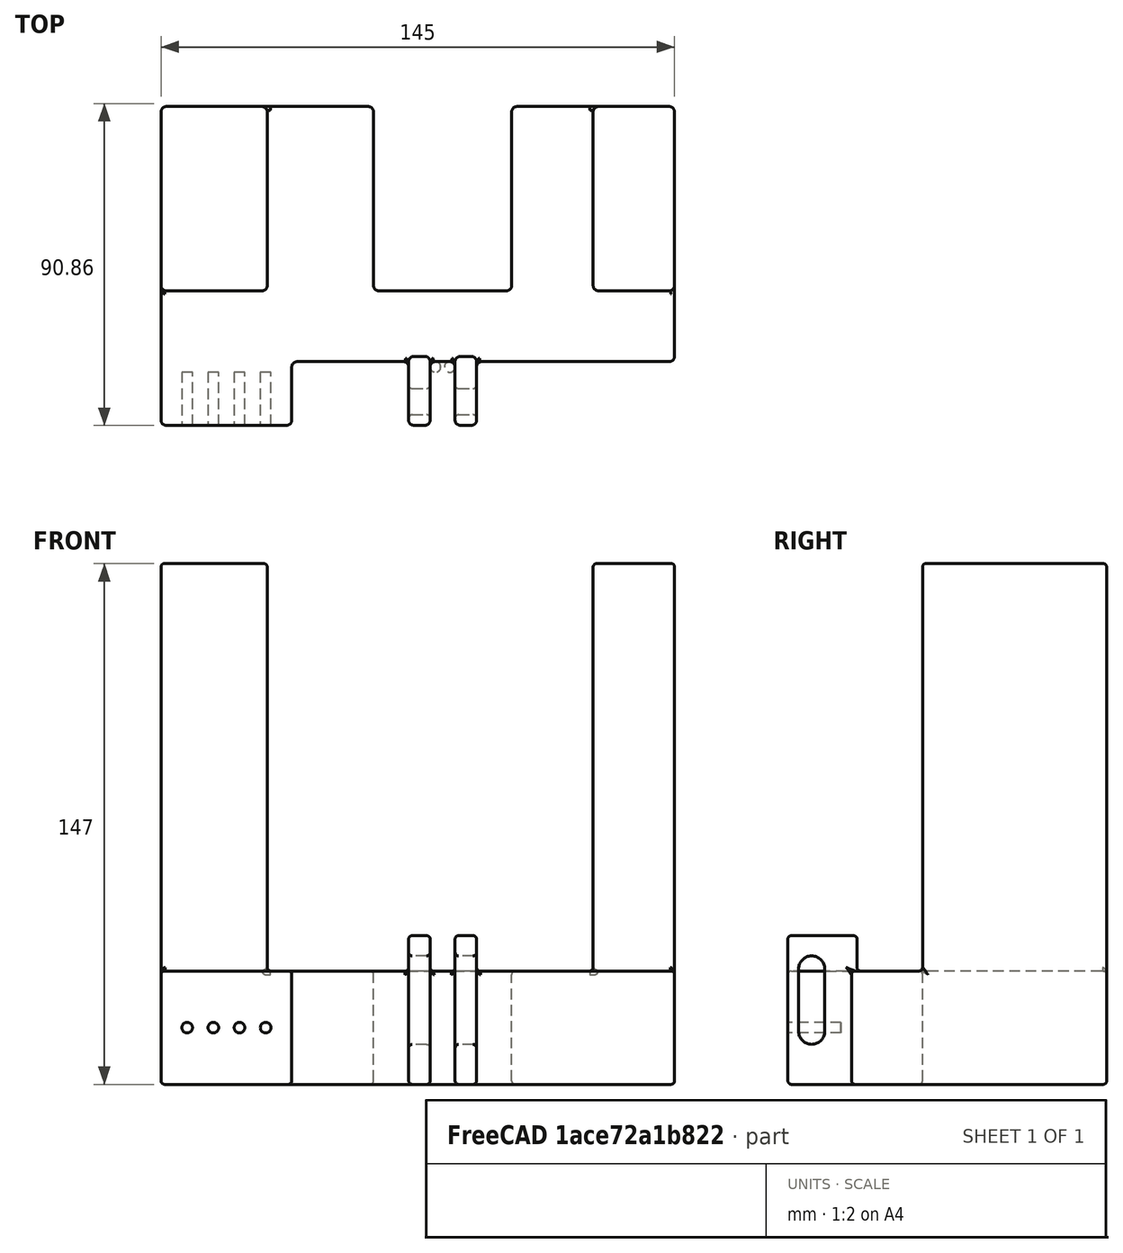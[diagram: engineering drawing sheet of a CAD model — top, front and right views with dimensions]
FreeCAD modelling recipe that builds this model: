
FCSTD DOCUMENT  (FreeCAD 1.0RUnknown)
Label: water-valve-support-v3
License: All rights reserved
LicenseURL: https://en.wikipedia.org/wiki/All_rights_reserved
objects: Sketcher::SketchObject×5, PartDesign::Pad×4, PartDesign::Fillet×4, PartDesign::Pocket×2, PartDesign::Body×1
note: 41 computed .brp shape members not serialized (recipe doc carries the construction recipe); baked Part::Feature solids carry a one-line shape summary decoded from their .brp

FEATURE [Sketcher::SketchObject] Sketch
  ArcFitTolerance = 1e-06
  AttachmentSupport = -> [XY_Plane]
  FullyConstrained = false
  MakeInternals = false
  MapMode = 5
  sketch-geometry (67):
    g0: LineSegment StartX=0 StartY=1.5 StartZ=0 EndX=0 EndY=38 EndZ=0
    g1: LineSegment StartX=0 StartY=38 StartZ=0 EndX=0 EndY=88.5 EndZ=0
    g2: LineSegment StartX=1.5 StartY=90 StartZ=0 EndX=58.5 EndY=90 EndZ=0
    g3: LineSegment StartX=60 StartY=88.5 StartZ=0 EndX=60 EndY=39.5 EndZ=0
    g4: LineSegment StartX=61.5 StartY=38 StartZ=0 EndX=97.5 EndY=38 EndZ=0
    g5: LineSegment StartX=99 StartY=39.5 StartZ=0 EndX=99 EndY=88.5 EndZ=0
    g6: LineSegment StartX=100.5 StartY=90 StartZ=0 EndX=143.5 EndY=90 EndZ=0
    g7: LineSegment StartX=145 StartY=88.5 StartZ=0 EndX=145 EndY=19.5 EndZ=0
    g8: LineSegment [constr] StartX=143.506 StartY=0 StartZ=0 EndX=118.575 EndY=0 EndZ=0
    g9: ArcOfCircle CenterX=1.5 CenterY=88.5 CenterZ=0 NormalX=0 NormalY=0 NormalZ=1 AngleXU=0 Radius=1.5 StartAngle=1.5708 EndAngle=3.14159
    g10: GeomPoint [constr] X=0 Y=90 Z=0
    g11: ArcOfCircle CenterX=58.5 CenterY=88.5 CenterZ=0 NormalX=0 NormalY=0 NormalZ=1 AngleXU=0 Radius=1.5 StartAngle=1.1e-15 EndAngle=1.5708
    g12: GeomPoint [constr] X=60 Y=90 Z=0
    g13: ArcOfCircle CenterX=61.5 CenterY=39.5 CenterZ=0 NormalX=0 NormalY=0 NormalZ=1 AngleXU=0 Radius=1.5 StartAngle=3.14159 EndAngle=4.71239
    g14: GeomPoint [constr] X=60 Y=38 Z=0
    g15: ArcOfCircle CenterX=97.5 CenterY=39.5 CenterZ=0 NormalX=0 NormalY=0 NormalZ=1 AngleXU=0 Radius=1.5 StartAngle=4.71239 EndAngle=6.28319
    g16: GeomPoint [constr] X=99 Y=38 Z=0
    g17: ArcOfCircle CenterX=100.5 CenterY=88.5 CenterZ=0 NormalX=0 NormalY=0 NormalZ=1 AngleXU=0 Radius=1.5 StartAngle=1.5708 EndAngle=3.14159
    g18: GeomPoint [constr] X=99 Y=90 Z=0
    g19: ArcOfCircle CenterX=143.5 CenterY=88.5 CenterZ=0 NormalX=0 NormalY=0 NormalZ=1 AngleXU=0 Radius=1.5 StartAngle=-4.4e-15 EndAngle=1.5708
    g20: GeomPoint [constr] X=145 Y=90 Z=0
    g21: ArcOfCircle [constr] CenterX=143.506 CenterY=1.5 CenterZ=0 NormalX=0 NormalY=0 NormalZ=1 AngleXU=0 Radius=1.5 StartAngle=4.71239 EndAngle=6.28336
    g22: GeomPoint [constr] X=145 Y=0 Z=0
    g23: ArcOfCircle CenterX=1.5 CenterY=1.5 CenterZ=0 NormalX=0 NormalY=0 NormalZ=1 AngleXU=0 Radius=1.5 StartAngle=3.14159 EndAngle=4.71239
    g24: GeomPoint [constr] X=0 Y=0 Z=0
    g25: GeomPoint [constr] X=79.5 Y=38 Z=0
    g26: LineSegment [constr] StartX=79.5 StartY=38 StartZ=0 EndX=79.5 EndY=0 EndZ=0
    g27: LineSegment StartX=75.975 StartY=1.5 StartZ=0 EndX=75.975 EndY=16.5 EndZ=0
    g28: LineSegment StartX=77.475 StartY=18 StartZ=0 EndX=81.525 EndY=18 EndZ=0
    g29: LineSegment StartX=83.025 StartY=1.5 StartZ=0 EndX=83.025 EndY=16.5 EndZ=0
    g30: GeomPoint [constr] X=79.5 Y=18 Z=0
    g31: LineSegment StartX=36.925 StartY=16.5 StartZ=0 EndX=36.925 EndY=1.5 EndZ=0
    g32: LineSegment StartX=69.925 StartY=1.5 StartZ=0 EndX=69.925 EndY=16.5 EndZ=0
    g33: LineSegment StartX=68.425 StartY=18 StartZ=0 EndX=38.425 EndY=18 EndZ=0
    g34: LineSegment StartX=89.075 StartY=16.5 StartZ=0 EndX=89.075 EndY=1.5 EndZ=0
    g35: LineSegment [constr] StartX=117.075 StartY=1.5 StartZ=0 EndX=117.075 EndY=16.5 EndZ=0
    g36: LineSegment StartX=115.575 StartY=18 StartZ=0 EndX=90.575 EndY=18 EndZ=0
    g37: LineSegment StartX=35.425 StartY=0 StartZ=0 EndX=1.5 EndY=0 EndZ=0
    g38: LineSegment StartX=74.475 StartY=0 StartZ=0 EndX=71.425 EndY=0 EndZ=0
    g39: LineSegment StartX=87.575 StartY=0 StartZ=0 EndX=84.525 EndY=0 EndZ=0
    g40: ArcOfCircle CenterX=35.425 CenterY=1.5 CenterZ=0 NormalX=0 NormalY=0 NormalZ=1 AngleXU=0 Radius=1.5 StartAngle=4.71239 EndAngle=6.28319
    g41: ArcOfCircle CenterX=71.425 CenterY=1.5 CenterZ=0 NormalX=0 NormalY=0 NormalZ=1 AngleXU=0 Radius=1.5 StartAngle=3.14159 EndAngle=4.71239
    g42: GeomPoint [constr] X=69.925 Y=0 Z=0
    g43: ArcOfCircle CenterX=74.475 CenterY=1.5 CenterZ=0 NormalX=0 NormalY=0 NormalZ=1 AngleXU=0 Radius=1.5 StartAngle=4.71239 EndAngle=6.28319
    g44: ArcOfCircle CenterX=84.525 CenterY=1.5 CenterZ=0 NormalX=0 NormalY=0 NormalZ=1 AngleXU=0 Radius=1.5 StartAngle=3.14159 EndAngle=4.71239
    g45: GeomPoint [constr] X=83.025 Y=0 Z=0
    g46: ArcOfCircle CenterX=87.575 CenterY=1.5 CenterZ=0 NormalX=0 NormalY=0 NormalZ=1 AngleXU=0 Radius=1.5 StartAngle=4.71239 EndAngle=6.28319
    g47: ArcOfCircle [constr] CenterX=118.575 CenterY=1.5 CenterZ=0 NormalX=0 NormalY=0 NormalZ=1 AngleXU=0 Radius=1.5 StartAngle=3.14159 EndAngle=4.71239
    g48: ArcOfCircle CenterX=38.425 CenterY=16.5 CenterZ=0 NormalX=0 NormalY=0 NormalZ=1 AngleXU=0 Radius=1.5 StartAngle=1.5708 EndAngle=3.14159
    g49: GeomPoint [constr] X=36.925 Y=18 Z=0
    g50: GeomPoint [constr] X=69.925 Y=18 Z=0
    g51: GeomPoint [constr] X=75.975 Y=18 Z=0
    g52: GeomPoint [constr] X=83.025 Y=18 Z=0
    g53: GeomPoint [constr] X=89.075 Y=18 Z=0
    g54: ArcOfCircle [constr] CenterX=115.575 CenterY=16.5 CenterZ=0 NormalX=0 NormalY=0 NormalZ=1 AngleXU=0 Radius=1.5 StartAngle=0 EndAngle=1.5708
    g55: GeomPoint [constr] X=117.075 Y=18 Z=0
    g56: ArcOfCircle CenterX=68.425 CenterY=16.5 CenterZ=0 NormalX=0 NormalY=0 NormalZ=1 AngleXU=0 Radius=1.5 StartAngle=0 EndAngle=1.5708
    g57: GeomPoint [constr] X=69.925 Y=18 Z=0
    g58: ArcOfCircle CenterX=77.475 CenterY=16.5 CenterZ=0 NormalX=0 NormalY=0 NormalZ=1 AngleXU=0 Radius=1.5 StartAngle=1.5708 EndAngle=3.14159
    g59: GeomPoint [constr] X=75.975 Y=18 Z=0
    g60: ArcOfCircle CenterX=81.525 CenterY=16.5 CenterZ=0 NormalX=0 NormalY=0 NormalZ=1 AngleXU=0 Radius=1.5 StartAngle=4e-16 EndAngle=1.5708
    g61: GeomPoint [constr] X=83.025 Y=18 Z=0
    g62: ArcOfCircle CenterX=90.575 CenterY=16.5 CenterZ=0 NormalX=0 NormalY=0 NormalZ=1 AngleXU=0 Radius=1.5 StartAngle=1.5708 EndAngle=3.14159
    g63: GeomPoint [constr] X=89.075 Y=18 Z=0
    g64: LineSegment StartX=115.575 StartY=18 StartZ=0 EndX=143.5 EndY=18 EndZ=0
    g65: ArcOfCircle CenterX=143.5 CenterY=19.5 CenterZ=0 NormalX=0 NormalY=0 NormalZ=1 AngleXU=0 Radius=1.5 StartAngle=4.71239 EndAngle=6.28319
    g66: LineSegment [constr] StartX=145 StartY=19.5 StartZ=0 EndX=145 EndY=1.36507 EndZ=0
  constraints (152):
    c: Coincident(g24,g-1)
    c: PointOnObject(g0,g-2)
    c: Vertical(g1)
    c: Horizontal(g2)
    c: Vertical(g3)
    c: Horizontal(g4)
    c: Vertical(g5)
    c: Horizontal(g6)
    c: Vertical(g7)
    c: PointOnObject(g22,g-1)
    c: Horizontal(g1,g14)
    c: DistanceX(g24,g22) = 145
    c: Distance(g24,g0) = 38
    c: DistanceX(g16,g22) = 46
    c: DistanceX(g14,g16) = 39
    c: Distance(g12,g14) = 52
    c: Coincident(g1,g0)
    c: PointOnObject(g10,g1)
    c: PointOnObject(g10,g2)
    c: Tangent(g1,g9) = 1.5708
    c: Tangent(g2,g9) = 1.5708
    c: PointOnObject(g12,g2)
    c: PointOnObject(g12,g3)
    c: Tangent(g2,g11) = 1.5708
    c: Tangent(g3,g11) = 1.5708
    c: PointOnObject(g14,g4)
    c: PointOnObject(g14,g3)
    c: Tangent(g4,g13) = -1.5708
    c: Tangent(g3,g13) = -1.5708
    c: PointOnObject(g16,g5)
    c: PointOnObject(g16,g4)
    c: Tangent(g5,g15) = -1.5708
    c: Tangent(g4,g15) = -1.5708
    c: PointOnObject(g18,g5)
    c: PointOnObject(g18,g6)
    c: Tangent(g5,g17) = 1.5708
    c: Tangent(g6,g17) = 1.5708
    c: PointOnObject(g20,g6)
    c: PointOnObject(g20,g7)
    c: Tangent(g6,g19) = 1.5708
    c: Tangent(g7,g19) = 1.5708
    c: PointOnObject(g22,g8)
    c: PointOnObject(g22,g7)
    c: Tangent(g8,g21) = 1.5708
    c: PointOnObject(g24,g37)
    c: PointOnObject(g24,g0)
    c: Coincident(g37,g23) = 1.5708
    c: Tangent(g0,g23) = 1.5708
    c: Equal(g9,g11)
    c: Equal(g11,g13)
    c: Equal(g13,g15)
    c: Equal(g15,g17)
    c: Equal(g17,g19)
    c: Equal(g19,g21)
    c: Equal(g21,g23)
    c: Radius(g9) = 1.5
    c: Horizontal(g11,g17)
    c: Symmetric(g4,g4,g25)
    c: Coincident(g26,g25)
    c: Vertical(g26)
    c: Vertical(g27)
    c: Horizontal(g28)
    c: Vertical(g29)
    c: Symmetric(g51,g52,g30)
    c: PointOnObject(g30,g26)
    c: Vertical(g31)
    c: Vertical(g32)
    c: Horizontal(g33)
    c: Vertical(g34)
    c: Vertical(g35)
    c: Horizontal(g36)
    c: Horizontal(g53,g30)
    c: Horizontal(g30,g50)
    c: Tangent(g37,g40) = 1.5708
    c: Tangent(g31,g40) = 1.5708
    c: PointOnObject(g42,g32)
    c: PointOnObject(g42,g38)
    c: Tangent(g32,g41) = 1.5708
    c: Tangent(g38,g41) = 1.5708
    c: Tangent(g38,g43) = 1.5708
    c: Tangent(g27,g43) = -1.5708
    c: PointOnObject(g45,g29)
    c: PointOnObject(g45,g39)
    c: Tangent(g29,g44) = 1.5708
    c: Tangent(g39,g44) = 1.5708
    c: Tangent(g39,g46) = 1.5708
    c: Tangent(g34,g46) = 1.5708
    c: Tangent(g35,g47) = 1.5708
    c: Tangent(g8,g47) = 1.5708
    c: PointOnObject(g49,g31)
    c: PointOnObject(g49,g33)
    c: Tangent(g31,g48) = -1.5708
    c: Tangent(g33,g48) = -1.5708
    c: PointOnObject(g53,g34)
    c: PointOnObject(g53,g36)
    c: PointOnObject(g55,g36)
    c: PointOnObject(g55,g35)
    c: Tangent(g36,g54) = -1.5708
    c: Tangent(g35,g54) = -1.5708
    c: Equal(g40,g48)
    c: Equal(g41,g43)
    c: Equal(g44,g46)
    c: Equal(g54,g47)
    c: Horizontal(g38)
    c: Horizontal(g8)
    c: Horizontal(g39)
    c: Horizontal(g39,g8)
    c: Horizontal(g8,g38)
    c: Horizontal(g38,g26)
    c: Horizontal(g37,g38)
    c: Equal(g40,g23)
    c: Equal(g38,g39)
    c: Distance(g27,g32) = 6.05
    c: Distance(g49,g-1) = 18
    c: Distance(g29,g27) = 7.05
    c: Coincident(g57,g50)
    c: Coincident(g59,g51)
    c: Coincident(g61,g52)
    c: Equal(g46,g41)
    c: Equal(g43,g40)
    c: Equal(g47,g48)
    c: PointOnObject(g57,g33)
    c: PointOnObject(g57,g32)
    c: Tangent(g33,g56) = -1.5708
    c: Tangent(g32,g56) = -1.5708
    c: PointOnObject(g59,g27)
    c: PointOnObject(g59,g28)
    c: Tangent(g27,g58) = 1.5708
    c: Tangent(g28,g58) = 1.5708
    c: PointOnObject(g61,g28)
    c: PointOnObject(g61,g29)
    c: Tangent(g28,g60) = 1.5708
    c: Tangent(g29,g60) = -1.5708
    c: PointOnObject(g63,g34)
    c: PointOnObject(g63,g36)
    c: Tangent(g34,g62) = -1.5708
    c: Tangent(g36,g62) = -1.5708
    c: Equal(g62,g60)
    c: Equal(g60,g58)
    c: Equal(g58,g56)
    c: Equal(g56,g41)
    c: DistanceX(g33,g33) = 30
    c: DistanceX(g36,g36) = 25
    c: Horizontal(g23,g40)
    c: Coincident(g64,g36)
    c: Horizontal(g64)
    c: Tangent(g7,g65) = 1.5708
    c: Tangent(g64,g65) = -1.5708
    c: Equal(g65,g54)
    c: Tangent(g66,g65) = 1.5708
    c: PointOnObject(g66,g21)
    c: Vertical(g66)
FEATURE [PartDesign::Pad] Pad
  Direction = (0,0,1)
  Length = 32
  Length2 = 10
  Profile = -> Sketch
  ReferenceAxis = -> Sketch [N_Axis]
  Refine = true
  Suppressed = false
  Type = 0
FEATURE [Sketcher::SketchObject] Sketch001
  ArcFitTolerance = 1e-06
  AttachmentSupport = -> [Pad]
  ExternalGeometry = -> [Pad]
  FullyConstrained = true
  MakeInternals = false
  MapMode = 5
  Placement = pos=(0,0,32) rot=(0,0,1;0rad)
  sketch-geometry (28):
    g0: LineSegment StartX=2.82e-13 StartY=88.5 StartZ=0 EndX=2.82e-13 EndY=39.5 EndZ=0
    g1: LineSegment StartX=1.5 StartY=38 StartZ=0 EndX=28.5 EndY=38 EndZ=0
    g2: LineSegment StartX=28.5 StartY=90 StartZ=0 EndX=1.5 EndY=90 EndZ=0
    g3: LineSegment StartX=123.5 StartY=38 StartZ=0 EndX=143.5 EndY=38 EndZ=0
    g4: LineSegment StartX=145 StartY=39.5 StartZ=0 EndX=145 EndY=88.5 EndZ=0
    g5: LineSegment StartX=143.5 StartY=90 StartZ=0 EndX=123.5 EndY=90 EndZ=0
    g6: ArcOfCircle CenterX=1.5 CenterY=88.5 CenterZ=0 NormalX=0 NormalY=0 NormalZ=1 AngleXU=0 Radius=1.5 StartAngle=1.5708 EndAngle=3.14159
    g7: GeomPoint [constr] X=6.1e-15 Y=90 Z=0
    g8: ArcOfCircle CenterX=1.5 CenterY=39.5 CenterZ=0 NormalX=0 NormalY=0 NormalZ=1 AngleXU=0 Radius=1.5 StartAngle=3.14159 EndAngle=4.71239
    g9: GeomPoint [constr] X=6.1e-15 Y=38 Z=0
    g10: ArcOfCircle CenterX=143.5 CenterY=88.5 CenterZ=0 NormalX=0 NormalY=0 NormalZ=1 AngleXU=0 Radius=1.5 StartAngle=3.04e-14 EndAngle=1.5708
    g11: GeomPoint [constr] X=145 Y=90 Z=0
    g12: ArcOfCircle CenterX=143.5 CenterY=39.5 CenterZ=0 NormalX=0 NormalY=0 NormalZ=1 AngleXU=0 Radius=1.5 StartAngle=4.71239 EndAngle=6.28319
    g13: GeomPoint [constr] X=145 Y=38 Z=0
    g14: GeomPoint [constr] X=30 Y=90 Z=0
    g15: GeomPoint [constr] X=122 Y=90 Z=0
    g16: LineSegment StartX=30 StartY=88.5 StartZ=0 EndX=30 EndY=39.5 EndZ=0
    g17: LineSegment StartX=122 StartY=88.5 StartZ=0 EndX=122 EndY=39.5 EndZ=0
    g18: GeomPoint [constr] X=30 Y=90 Z=0
    g19: GeomPoint [constr] X=122 Y=90 Z=0
    g20: ArcOfCircle CenterX=28.5 CenterY=88.5 CenterZ=0 NormalX=0 NormalY=0 NormalZ=1 AngleXU=0 Radius=1.5 StartAngle=1.119e-13 EndAngle=1.5708
    g21: GeomPoint [constr] X=30 Y=90 Z=0
    g22: ArcOfCircle CenterX=28.5 CenterY=39.5 CenterZ=0 NormalX=0 NormalY=0 NormalZ=1 AngleXU=0 Radius=1.5 StartAngle=4.71239 EndAngle=6.28319
    g23: GeomPoint [constr] X=30 Y=38 Z=0
    g24: ArcOfCircle CenterX=123.5 CenterY=88.5 CenterZ=0 NormalX=0 NormalY=0 NormalZ=1 AngleXU=0 Radius=1.5 StartAngle=1.5708 EndAngle=3.14159
    g25: GeomPoint [constr] X=122 Y=90 Z=0
    g26: ArcOfCircle CenterX=123.5 CenterY=39.5 CenterZ=0 NormalX=0 NormalY=0 NormalZ=1 AngleXU=0 Radius=1.5 StartAngle=3.14159 EndAngle=4.71239
    g27: GeomPoint [constr] X=122 Y=38 Z=0
  constraints (56):
    c: Vertical(g0)
    c: Horizontal(g1)
    c: Horizontal(g2)
    c: Vertical(g4)
    c: Horizontal(g3)
    c: Horizontal(g5)
    c: PointOnObject(g7,g0)
    c: PointOnObject(g7,g2)
    c: Tangent(g0,g6) = -1.5708
    c: Tangent(g2,g6) = -1.5708
    c: PointOnObject(g9,g0)
    c: PointOnObject(g9,g1)
    c: Tangent(g0,g8) = -1.5708
    c: Tangent(g1,g8) = -1.5708
    c: PointOnObject(g11,g4)
    c: PointOnObject(g11,g5)
    c: Tangent(g4,g10) = -1.5708
    c: Tangent(g5,g10) = -1.5708
    c: PointOnObject(g13,g3)
    c: PointOnObject(g13,g4)
    c: Tangent(g3,g12) = -1.5708
    c: Tangent(g4,g12) = -1.5708
    c: Coincident(g6,g-4)
    c: Coincident(g10,g-14)
    c: Coincident(g21,g14)
    c: Coincident(g25,g15)
    c: Symmetric(g-3,g-3,g18)
    c: Symmetric(g-13,g-13,g19)
    c: Coincident(g21,g18)
    c: Vertical(g16)
    c: Horizontal(g27,g-10)
    c: Horizontal(g-10,g23)
    c: Coincident(g15,g19)
    c: Vertical(g17)
    c: PointOnObject(g21,g2)
    c: PointOnObject(g21,g16)
    c: Tangent(g2,g20) = -1.5708
    c: Tangent(g16,g20) = 1.5708
    c: PointOnObject(g23,g16)
    c: PointOnObject(g23,g1)
    c: Tangent(g16,g22) = 1.5708
    c: Tangent(g1,g22) = -1.5708
    c: PointOnObject(g25,g17)
    c: PointOnObject(g25,g5)
    c: Tangent(g17,g24) = -1.5708
    c: Tangent(g5,g24) = -1.5708
    c: PointOnObject(g27,g3)
    c: PointOnObject(g27,g17)
    c: Tangent(g3,g26) = -1.5708
    c: Tangent(g17,g26) = -1.5708
    c: Equal(g20,g8)
    c: Equal(g8,g22)
    c: Equal(g22,g24)
    c: Equal(g24,g26)
    c: Equal(g26,g12)
    c: Equal(g12,g6)
FEATURE [PartDesign::Pad] Pad001
  BaseFeature = -> Pad
  Direction = (0,0,1)
  Length = 115
  Length2 = 10
  Profile = -> Sketch001
  ReferenceAxis = -> Sketch001 [N_Axis]
  Refine = true
  Suppressed = false
  Type = 0
FEATURE [Sketcher::SketchObject] Sketch002
  ArcFitTolerance = 1e-06
  AttachmentSupport = -> [Pad001]
  ExternalGeometry = -> [Pad001]
  FullyConstrained = true
  MakeInternals = false
  MapMode = 5
  Placement = pos=(0,0,32) rot=(0,0,1;0rad)
  sketch-geometry (24):
    g0: LineSegment StartX=69.925 StartY=18 StartZ=0 EndX=69.925 EndY=1.5 EndZ=0
    g1: LineSegment StartX=71.425 StartY=-5.8e-15 StartZ=0 EndX=74.475 EndY=-5.8e-15 EndZ=0
    g2: LineSegment StartX=75.975 StartY=1.5 StartZ=0 EndX=75.975 EndY=18 EndZ=0
    g3: LineSegment StartX=74.475 StartY=19.5 StartZ=0 EndX=71.425 EndY=19.5 EndZ=0
    g4: LineSegment StartX=83.025 StartY=18 StartZ=0 EndX=83.025 EndY=1.5 EndZ=0
    g5: LineSegment StartX=84.525 StartY=-5.8e-15 StartZ=0 EndX=87.575 EndY=-5.8e-15 EndZ=0
    g6: LineSegment StartX=89.075 StartY=1.5 StartZ=0 EndX=89.075 EndY=18 EndZ=0
    g7: LineSegment StartX=87.575 StartY=19.5 StartZ=0 EndX=84.525 EndY=19.5 EndZ=0
    g8: ArcOfCircle CenterX=71.425 CenterY=18 CenterZ=0 NormalX=0 NormalY=0 NormalZ=1 AngleXU=0 Radius=1.5 StartAngle=1.5708 EndAngle=3.14159
    g9: GeomPoint [constr] X=69.925 Y=19.5 Z=0
    g10: ArcOfCircle CenterX=74.475 CenterY=18 CenterZ=0 NormalX=0 NormalY=0 NormalZ=1 AngleXU=0 Radius=1.5 StartAngle=-9e-16 EndAngle=1.5708
    g11: GeomPoint [constr] X=75.975 Y=19.5 Z=0
    g12: ArcOfCircle CenterX=84.525 CenterY=18 CenterZ=0 NormalX=0 NormalY=0 NormalZ=1 AngleXU=0 Radius=1.5 StartAngle=1.5708 EndAngle=3.14159
    g13: GeomPoint [constr] X=83.025 Y=19.5 Z=0
    g14: ArcOfCircle CenterX=87.575 CenterY=18 CenterZ=0 NormalX=0 NormalY=0 NormalZ=1 AngleXU=0 Radius=1.5 StartAngle=7e-16 EndAngle=1.5708
    g15: GeomPoint [constr] X=89.075 Y=19.5 Z=0
    g16: ArcOfCircle CenterX=87.575 CenterY=1.5 CenterZ=0 NormalX=0 NormalY=0 NormalZ=1 AngleXU=0 Radius=1.5 StartAngle=4.71239 EndAngle=6.28319
    g17: GeomPoint [constr] X=89.075 Y=-5.8e-15 Z=0
    g18: ArcOfCircle CenterX=84.525 CenterY=1.5 CenterZ=0 NormalX=0 NormalY=0 NormalZ=1 AngleXU=0 Radius=1.5 StartAngle=3.14159 EndAngle=4.71239
    g19: GeomPoint [constr] X=83.025 Y=-5.8e-15 Z=0
    g20: ArcOfCircle CenterX=74.475 CenterY=1.5 CenterZ=0 NormalX=0 NormalY=0 NormalZ=1 AngleXU=0 Radius=1.5 StartAngle=4.71239 EndAngle=6.28319
    g21: GeomPoint [constr] X=75.975 Y=-5.8e-15 Z=0
    g22: ArcOfCircle CenterX=71.425 CenterY=1.5 CenterZ=0 NormalX=0 NormalY=0 NormalZ=1 AngleXU=0 Radius=1.5 StartAngle=3.14159 EndAngle=4.71239
    g23: GeomPoint [constr] X=69.925 Y=-5.8e-15 Z=0
  constraints (51):
    c: Vertical(g0)
    c: Horizontal(g1)
    c: Horizontal(g3)
    c: Vertical(g4)
    c: Vertical(g6)
    c: Horizontal(g5)
    c: Horizontal(g7)
    c: PointOnObject(g9,g0)
    c: PointOnObject(g9,g3)
    c: Tangent(g0,g8) = -1.5708
    c: Tangent(g3,g8) = -1.5708
    c: PointOnObject(g11,g3)
    c: PointOnObject(g11,g2)
    c: Tangent(g3,g10) = -1.5708
    c: Tangent(g2,g10) = -1.5708
    c: PointOnObject(g13,g4)
    c: PointOnObject(g13,g7)
    c: Tangent(g4,g12) = -1.5708
    c: Tangent(g7,g12) = -1.5708
    c: PointOnObject(g15,g7)
    c: PointOnObject(g15,g6)
    c: Tangent(g7,g14) = -1.5708
    c: Tangent(g6,g14) = -1.5708
    c: PointOnObject(g17,g6)
    c: PointOnObject(g17,g5)
    c: Tangent(g6,g16) = -1.5708
    c: Tangent(g5,g16) = -1.5708
    c: PointOnObject(g19,g4)
    c: PointOnObject(g19,g5)
    c: Tangent(g4,g18) = -1.5708
    c: Tangent(g5,g18) = -1.5708
    c: PointOnObject(g21,g2)
    c: PointOnObject(g21,g1)
    c: Tangent(g2,g20) = -1.5708
    c: Tangent(g1,g20) = -1.5708
    c: PointOnObject(g23,g0)
    c: PointOnObject(g23,g1)
    c: Tangent(g0,g22) = -1.5708
    c: Tangent(g1,g22) = -1.5708
    c: Equal(g22,g8)
    c: Equal(g8,g10)
    c: Equal(g20,g18)
    c: Equal(g16,g12)
    c: Equal(g12,g14)
    c: Equal(g2,g4)
    c: Coincident(g20,g-6)
    c: Coincident(g-4,g22)
    c: Coincident(g18,g-10)
    c: Coincident(g16,g-12)
    c: Coincident(g2,g-7)
    c: Horizontal(g2,g-8)
FEATURE [PartDesign::Pad] Pad002
  BaseFeature = -> Pad001
  Direction = (0,0,1)
  Length = 10
  Length2 = 10
  Profile = -> Sketch002
  ReferenceAxis = -> Sketch002 [N_Axis]
  Refine = true
  Suppressed = false
  Type = 0
FEATURE [PartDesign::Pad] Pad003
  BaseFeature = -> Pad002
  Direction = (0,0,1)
  Length = 4.15
  Length2 = 10
  Profile = -> Sketch002
  ReferenceAxis = -> Sketch002 [N_Axis]
  Refine = true
  Suppressed = false
  Type = 0
FEATURE [Sketcher::SketchObject] Sketch003
  ArcFitTolerance = 1e-06
  AttachmentSupport = -> [Pad003]
  ExternalGeometry = -> [Pad003]
  FullyConstrained = true
  MakeInternals = false
  MapMode = 5
  Placement = pos=(69.925,0,0) rot=(0.57735,-0.57735,-0.57735;2.0944rad)
  sketch-geometry (5):
    g0: GeomPoint [constr] X=-6.7 Y=42 Z=0
    g1: ArcOfCircle CenterX=-6.7 CenterY=32.55 CenterZ=0 NormalX=0 NormalY=0 NormalZ=1 AngleXU=0 Radius=3.7 StartAngle=-9e-16 EndAngle=3.14159
    g2: ArcOfCircle CenterX=-6.7 CenterY=15 CenterZ=0 NormalX=0 NormalY=0 NormalZ=1 AngleXU=0 Radius=3.7 StartAngle=3.14159 EndAngle=6.28319
    g3: LineSegment StartX=-3 StartY=32.55 StartZ=0 EndX=-3 EndY=15 EndZ=0
    g4: LineSegment StartX=-10.4 StartY=32.55 StartZ=0 EndX=-10.4 EndY=15 EndZ=0
  constraints (12):
    c: PointOnObject(g0,g-3)
    c: Distance(g0,g-2) = 6.7
    c: Tangent(g1,g3) = 1.5708
    c: Tangent(g1,g4) = -1.5708
    c: Tangent(g2,g3) = 1.5708
    c: Tangent(g2,g4) = -1.5708
    c: Equal(g1,g2)
    c: Vertical(g4)
    c: Radius(g1) = 3.7
    c: Vertical(g1,g0)
    c: Distance(g1,g-3) = 9.45
    c: Distance(g2,g-1) = 15
FEATURE [PartDesign::Pocket] Pocket
  BaseFeature = -> Pad003
  Direction = (1,0,0)
  Length = 0
  Length2 = 5
  Profile = -> Sketch003
  ReferenceAxis = -> Sketch003 [N_Axis]
  Refine = true
  Suppressed = false
  Type = 3
  UpToFace = -> Pad003 [Face41]
FEATURE [Sketcher::SketchObject] Sketch004
  ArcFitTolerance = 1e-06
  AttachmentSupport = -> [Pocket]
  ExternalGeometry = -> [Pocket]
  FullyConstrained = true
  MakeInternals = false
  MapMode = 5
  Placement = pos=(0,0,0) rot=(1,0,0;1.5708rad)
  sketch-geometry (10):
    g0: GeomPoint [constr] X=0 Y=16 Z=0
    g1: Circle CenterX=7.385 CenterY=16 CenterZ=0 NormalX=0 NormalY=0 NormalZ=1 AngleXU=0 Radius=1.5
    g2: Circle CenterX=14.77 CenterY=16 CenterZ=0 NormalX=0 NormalY=0 NormalZ=1 AngleXU=0 Radius=1.5
    g3: Circle CenterX=22.155 CenterY=16 CenterZ=0 NormalX=0 NormalY=0 NormalZ=1 AngleXU=0 Radius=1.5
    g4: Circle CenterX=29.54 CenterY=16 CenterZ=0 NormalX=0 NormalY=0 NormalZ=1 AngleXU=0 Radius=1.5
    g5: LineSegment [constr] StartX=0 StartY=16 StartZ=0 EndX=7.385 EndY=16 EndZ=0
    g6: LineSegment [constr] StartX=7.385 StartY=16 StartZ=0 EndX=14.77 EndY=16 EndZ=0
    g7: LineSegment [constr] StartX=14.77 StartY=16 StartZ=0 EndX=22.155 EndY=16 EndZ=0
    g8: LineSegment [constr] StartX=22.155 StartY=16 StartZ=0 EndX=29.54 EndY=16 EndZ=0
    g9: LineSegment [constr] StartX=29.54 StartY=16 StartZ=0 EndX=36.925 EndY=16 EndZ=0
  constraints (23):
    c: Symmetric(g-3,g-3,g0)
    c: Diameter(g1) = 3
    c: Equal(g1,g2)
    c: Equal(g2,g3)
    c: Equal(g3,g4)
    c: Coincident(g5,g0)
    c: Coincident(g5,g1)
    c: Horizontal(g5)
    c: Coincident(g6,g1)
    c: Coincident(g6,g2)
    c: Horizontal(g6)
    c: Coincident(g7,g2)
    c: Coincident(g7,g3)
    c: Horizontal(g7)
    c: Coincident(g8,g3)
    c: Coincident(g8,g4)
    c: Horizontal(g8)
    c: Coincident(g9,g4)
    c: Symmetric(g-4,g-4,g9)
    c: Equal(g5,g6)
    c: Equal(g6,g7)
    c: Equal(g7,g8)
    c: Equal(g8,g9)
FEATURE [PartDesign::Pocket] Pocket001
  BaseFeature = -> Pocket
  Direction = (0,1,-2e-16)
  Length = 15
  Length2 = 5
  Profile = -> Sketch004
  ReferenceAxis = -> Sketch004 [N_Axis]
  Refine = true
  Suppressed = false
  Type = 0
FEATURE [PartDesign::Fillet] Fillet
  Base = -> Pocket001 [Edge121,Edge93,Edge97,Edge125,Edge29,Edge21,Edge84,Edge112]
  BaseFeature = -> Pocket001
  Radius = 1
  Refine = true
  SupportTransform = false
  Suppressed = false
  UseAllEdges = false
FEATURE [PartDesign::Fillet] Fillet001
  Base = -> Fillet [Edge237,Edge234]
  BaseFeature = -> Fillet
  Radius = 1
  Refine = true
  SupportTransform = false
  Suppressed = false
  UseAllEdges = false
FEATURE [PartDesign::Fillet] Fillet002
  Base = -> Fillet001 [Edge71,Edge58,Edge47]
  BaseFeature = -> Fillet001
  Radius = 1
  Refine = true
  SupportTransform = false
  Suppressed = false
  UseAllEdges = false
FEATURE [PartDesign::Fillet] Fillet003
  Base = -> Fillet002 [Edge56,Edge47,Edge32,Edge116,Edge168]
  BaseFeature = -> Fillet002
  Radius = 1
  Refine = true
  SupportTransform = false
  Suppressed = false
  UseAllEdges = false
FEATURE [PartDesign::Body] Body
  AllowCompound = false
  Group = -> [Sketch,Pad,Sketch001,Pad001,Sketch002,Pad002,Pad003,Sketch003,Pocket,Sketch004,Pocket001,Fillet,Fillet001,Fillet002,Fillet003]
  Origin = -> Origin
  Tip = -> Fillet003
